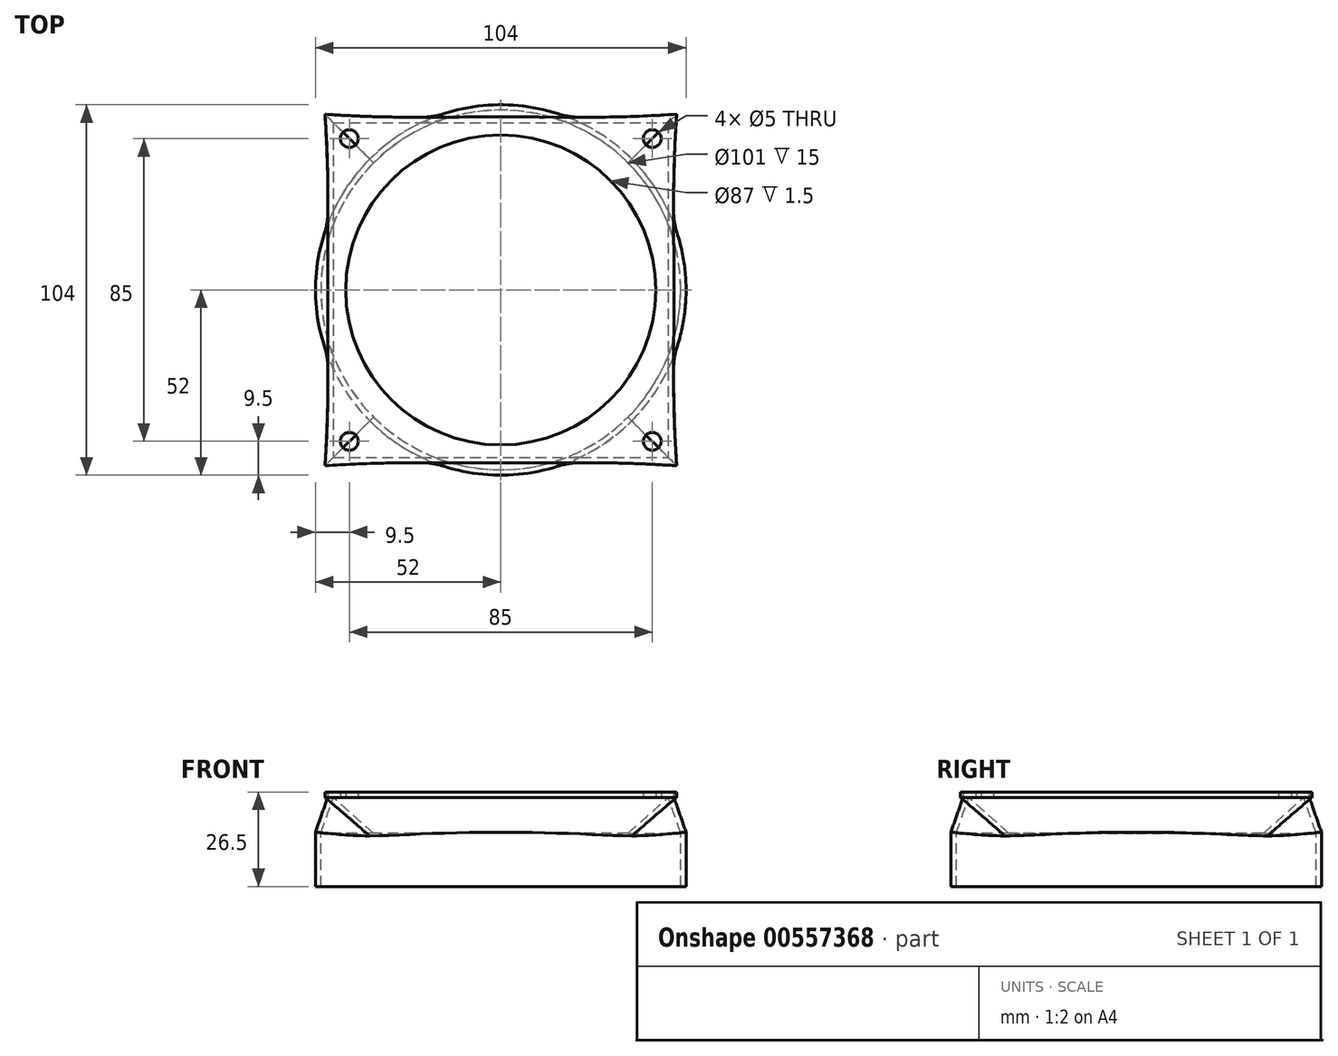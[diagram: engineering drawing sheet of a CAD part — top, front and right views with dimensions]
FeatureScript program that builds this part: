
annotation { "Feature Type Name" : "Feature", "Feature Type Description" : "" }
export const myFeature = defineFeature(function(context is Context, id is Id, definition is map)
    precondition{}
    {
        {
            var Q0;
            Q0=qCreatedBy(makeId("Top.planeOp"),FACE);
            var sketch = newSketch(context, id + "F0", { "sketchPlane" : qUnion([Q0])});
            skCircle(sketch, "E0", {"center": v(0, 0) * mm, "radius": 50.5 * mm});
            skSolve(sketch);
        }
        {
            var Q0;
            Q0=makeQuery(id+"F0.imprint","IMPRINT",FACE,{"disambiguationData":[TD([[makeQuery(id+"F0.imprint","IMPRINT",EDGE,{"derivedFrom":sQuery(id+"F0.wireOp",EDGE,"E0")}),1.0]])]});
            cPlane(context, id + "F1", {"entities" : qUnion([Q0]), "cplaneType" : CPlaneType.OFFSET, "offset" : 10 * mm, "width" : 150 * mm, "height" : 150 * mm});
        }
        {
            var Q0;
            Q0=qCreatedBy(id+"F1.planeOp",FACE);
            var sketch = newSketch(context, id + "F2", { "sketchPlane" : qUnion([Q0])});
            skLineSegment(sketch, "E1.bottom", {"start": v(-47, 47) * mm, "end": v(47, 47) * mm});
            skLineSegment(sketch, "E1.top", {"start": v(-47, -47) * mm, "end": v(47, -47) * mm});
            skLineSegment(sketch, "E1.left", {"start": v(-47, 47) * mm, "end": v(-47, -47) * mm});
            skLineSegment(sketch, "E1.right", {"start": v(47, 47) * mm, "end": v(47, -47) * mm});
            skPoint(sketch, "E1.middle", {"position": v(0, 0) * mm});
            skSolve(sketch);
        }
        {
            var Q0;
            Q0=makeQuery(id+"F0.imprint","IMPRINT",FACE,{"disambiguationData":[TD([[makeQuery(id+"F0.imprint","IMPRINT",EDGE,{"derivedFrom":sQuery(id+"F0.wireOp",EDGE,"E0")}),1.0]])]});
            var Q1;
            Q1=makeQuery(id+"F2.imprint","IMPRINT",FACE,{"disambiguationData":[TD([[makeQuery(id+"F2.imprint","IMPRINT",EDGE,{"derivedFrom":sQuery(id+"F2.wireOp",EDGE,"E1.bottom")}),-1.0]])]});
            var Q2;
            Q2=makeQuery(id+"F0.imprint","IMPRINT",FACE,{"disambiguationData":[TD([[makeQuery(id+"F0.imprint","IMPRINT",EDGE,{"derivedFrom":sQuery(id+"F0.wireOp",EDGE,"E0")}),1.0]])]});
            var Q3;
            Q3=makeQuery(id+"F2.imprint","IMPRINT",FACE,{"disambiguationData":[TD([[makeQuery(id+"F2.imprint","IMPRINT",EDGE,{"derivedFrom":sQuery(id+"F2.wireOp",EDGE,"E1.bottom")}),-1.0]])]});
            loft(context, id + "F3", {"sheetProfilesArray" : [{ "sheetProfileEntities" : qUnion([Q0]) }, { "sheetProfileEntities" : qUnion([Q1]) }], "wireProfilesArray" : [{ "wireProfileEntities" : qUnion([Q2]) }, { "wireProfileEntities" : qUnion([Q3]) }]});
        }
        {
            var Q0;
            Q0=qSketchRegion(id+"F0",true);
            extrude(context, id + "F4", {"entities" : qUnion([Q0]), "operationType" : NewBodyOperationType.ADD, "oppositeDirection" : true, "depth" : 15 * mm, "offsetDistance" : 25 * mm});
        }
        {
            var Q0;
            Q0=makeQuery(id+"F4.opExtrude","CAP_FACE",FACE,{"disambiguationData":[OSD([sQuery(id+"F0.wireOp",EDGE,"E0")])],"isStart":false});
            var Q1;
            Q1=makeQuery(id+"F3.opLoft","CAP_FACE",FACE,{"disambiguationData":[OSD([makeQuery(id+"F2.imprint","IMPRINT",FACE,{"disambiguationData":[TD([[makeQuery(id+"F2.imprint","IMPRINT",EDGE,{"derivedFrom":sQuery(id+"F2.wireOp",EDGE,"E1.bottom")}),-1.0]])]})])],"isStart":true});
            shell(context, id + "F5", {"entities" : qUnion([Q0, Q1]), "thickness" : 1.5 * mm, "oppositeDirection" : true});
        }
        {
            var Q0;
            Q0=makeQuery(id+"F3.opLoft","CAP_FACE",FACE,{"disambiguationData":[OSD([makeQuery(id+"F2.imprint","IMPRINT",FACE,{"disambiguationData":[TD([[makeQuery(id+"F2.imprint","IMPRINT",EDGE,{"derivedFrom":sQuery(id+"F2.wireOp",EDGE,"E1.bottom")}),-1.0]])]})])],"isStart":true});
            var sketch = newSketch(context, id + "F6", { "sketchPlane" : qUnion([Q0])});
            skLineSegment(sketch, "E2.bottom", {"start": v(-47, 47) * mm, "end": v(47, 47) * mm});
            skLineSegment(sketch, "E2.top", {"start": v(-47, -47) * mm, "end": v(47, -47) * mm});
            skLineSegment(sketch, "E2.left", {"start": v(-47, 47) * mm, "end": v(-47, -47) * mm});
            skLineSegment(sketch, "E2.right", {"start": v(47, 47) * mm, "end": v(47, -47) * mm});
            skPoint(sketch, "E2.middle", {"position": v(0, 0) * mm});
            skCircle(sketch, "E3", {"center": v(-42.5, 42.5) * mm, "radius": 2.5 * mm});
            skLineSegment(sketch, "E4", {"start": v(0, 0) * mm, "end": v(0, 23.14) * mm, "construction": true});
            skLineSegment(sketch, "E5", {"start": v(0, 23.14) * mm, "end": v(0, 0) * mm, "construction": true});
            skLineSegment(sketch, "E6", {"start": v(26.08, 0) * mm, "end": v(0, 0) * mm, "construction": true});
            skCircle(sketch, "E7.MirrorC", {"center": v(42.5, 42.5) * mm, "radius": 2.5 * mm});
            skCircle(sketch, "E8.MirrorC", {"center": v(-42.5, -42.5) * mm, "radius": 2.5 * mm});
            skCircle(sketch, "E9.MirrorC", {"center": v(42.5, -42.5) * mm, "radius": 2.5 * mm});
            skCircle(sketch, "E10", {"center": v(0, 0) * mm, "radius": 43.5 * mm});
            skLineSegment(sketch, "E11.bottom", {"start": v(-49.33, 49.33) * mm, "end": v(49.33, 49.33) * mm});
            skLineSegment(sketch, "E11.top", {"start": v(-49.33, -49.33) * mm, "end": v(49.33, -49.33) * mm});
            skLineSegment(sketch, "E11.left", {"start": v(-49.33, 49.33) * mm, "end": v(-49.33, -49.33) * mm});
            skLineSegment(sketch, "E11.right", {"start": v(49.33, 49.33) * mm, "end": v(49.33, -49.33) * mm});
            skSolve(sketch);
        }
        {
            var Q0;
            Q0=makeQuery(id+"F6.imprint","IMPRINT",FACE,{"disambiguationData":[TD([[makeQuery(id+"F6.imprint","IMPRINT",EDGE,{"derivedFrom":sQuery(id+"F6.wireOp",EDGE,"E2.bottom")}),1.0]])]});
            var Q1;
            Q1=makeQuery(id+"F6.imprint","IMPRINT",FACE,{"disambiguationData":[TD([[makeQuery(id+"F6.imprint","IMPRINT",EDGE,{"derivedFrom":sQuery(id+"F6.wireOp",EDGE,"E2.bottom")}),-1.0]])]});
            extrude(context, id + "F7", {"entities" : qUnion([Q0, Q1]), "operationType" : NewBodyOperationType.ADD, "depth" : 1.5 * mm, "offsetDistance" : 25 * mm});
        }
    });
